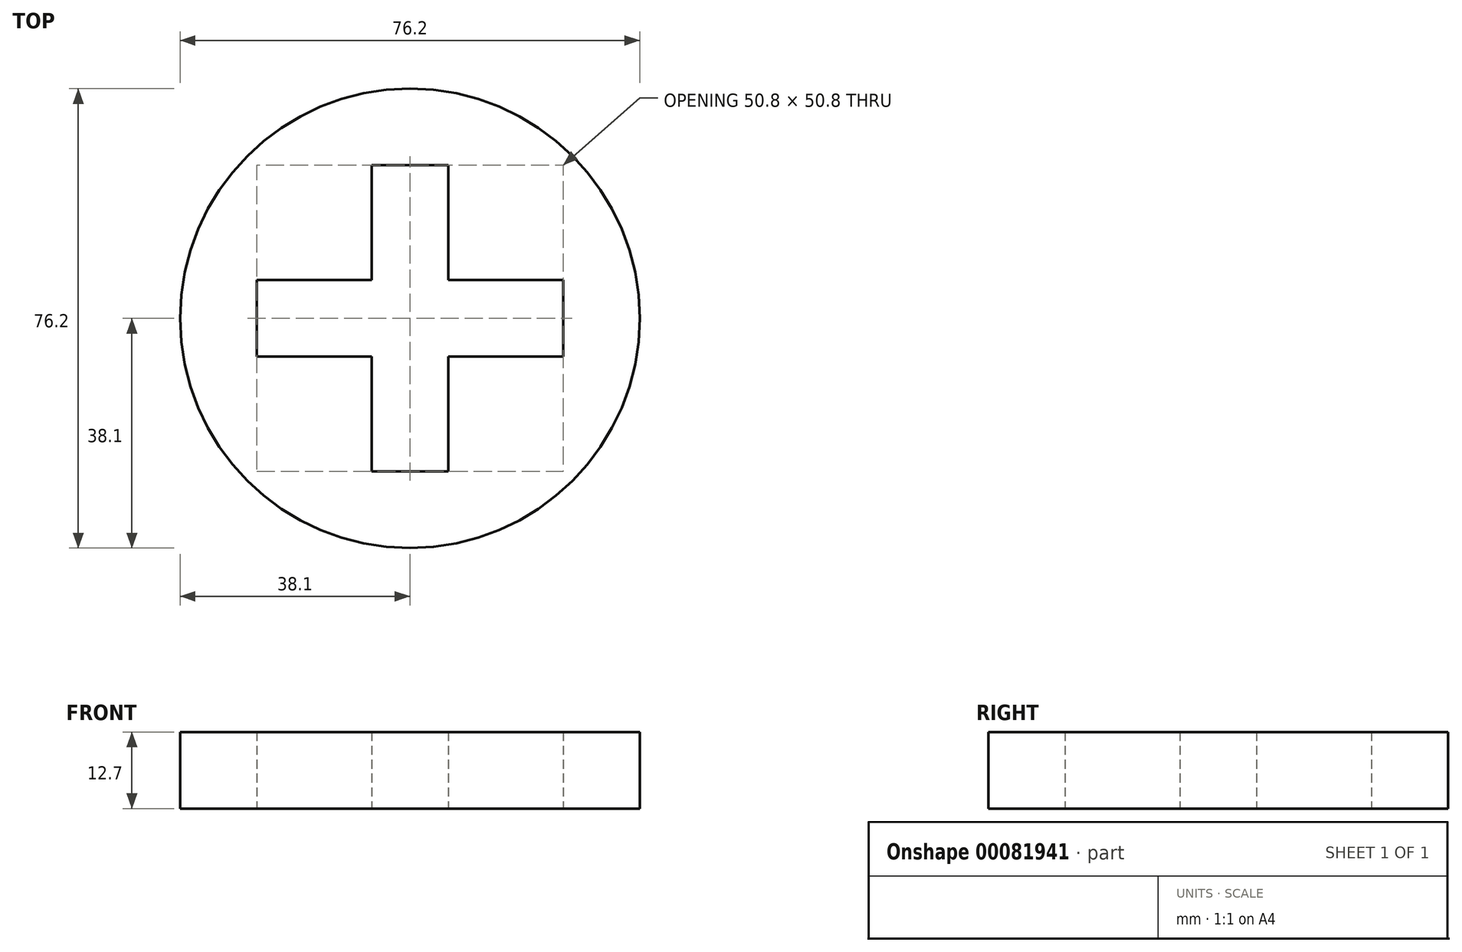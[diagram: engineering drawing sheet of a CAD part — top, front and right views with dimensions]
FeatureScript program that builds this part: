
annotation { "Feature Type Name" : "Feature", "Feature Type Description" : "" }
export const myFeature = defineFeature(function(context is Context, id is Id, definition is map)
    precondition{}
    {
        {
            var Q0;
            Q0=qCreatedBy(makeId("Top.planeOp"),FACE);
            var sketch = newSketch(context, id + "F0", { "sketchPlane" : qUnion([Q0])});
            skCircle(sketch, "E0", {"center": v(0, 0) * mm, "radius": 38.1 * mm});
            skLineSegment(sketch, "E1", {"start": v(6.35, 6.35) * mm, "end": v(6.35, 25.4) * mm});
            skLineSegment(sketch, "E2", {"start": v(6.35, 25.4) * mm, "end": v(-6.35, 25.4) * mm});
            skLineSegment(sketch, "E3", {"start": v(-6.35, 25.4) * mm, "end": v(-6.35, 6.35) * mm});
            skLineSegment(sketch, "E4", {"start": v(-6.35, -25.4) * mm, "end": v(6.35, -25.4) * mm});
            skLineSegment(sketch, "E5", {"start": v(6.35, -6.35) * mm, "end": v(6.35, -25.4) * mm});
            skLineSegment(sketch, "E6", {"start": v(6.35, 6.35) * mm, "end": v(25.4, 6.35) * mm});
            skLineSegment(sketch, "E7", {"start": v(25.4, 6.35) * mm, "end": v(25.4, -6.35) * mm});
            skLineSegment(sketch, "E8", {"start": v(25.4, -6.35) * mm, "end": v(6.35, -6.35) * mm});
            skLineSegment(sketch, "E9", {"start": v(-25.4, -6.35) * mm, "end": v(-25.4, 6.35) * mm});
            skLineSegment(sketch, "E10", {"start": v(-25.4, 6.35) * mm, "end": v(-6.35, 6.35) * mm});
            skLineSegment(sketch, "E11.trimOffspring", {"start": v(-6.35, -6.35) * mm, "end": v(-25.4, -6.35) * mm});
            skLineSegment(sketch, "E12.trimOffspring", {"start": v(-6.35, -6.35) * mm, "end": v(-6.35, -25.4) * mm});
            skSolve(sketch);
        }
        {
            var Q0;
            Q0 = qSketchRegion(id + "F0", true);
            extrude(context, id + "F1", {"entities" : qUnion([Q0]), "depth" : 12.7 * mm});
        }
    });
